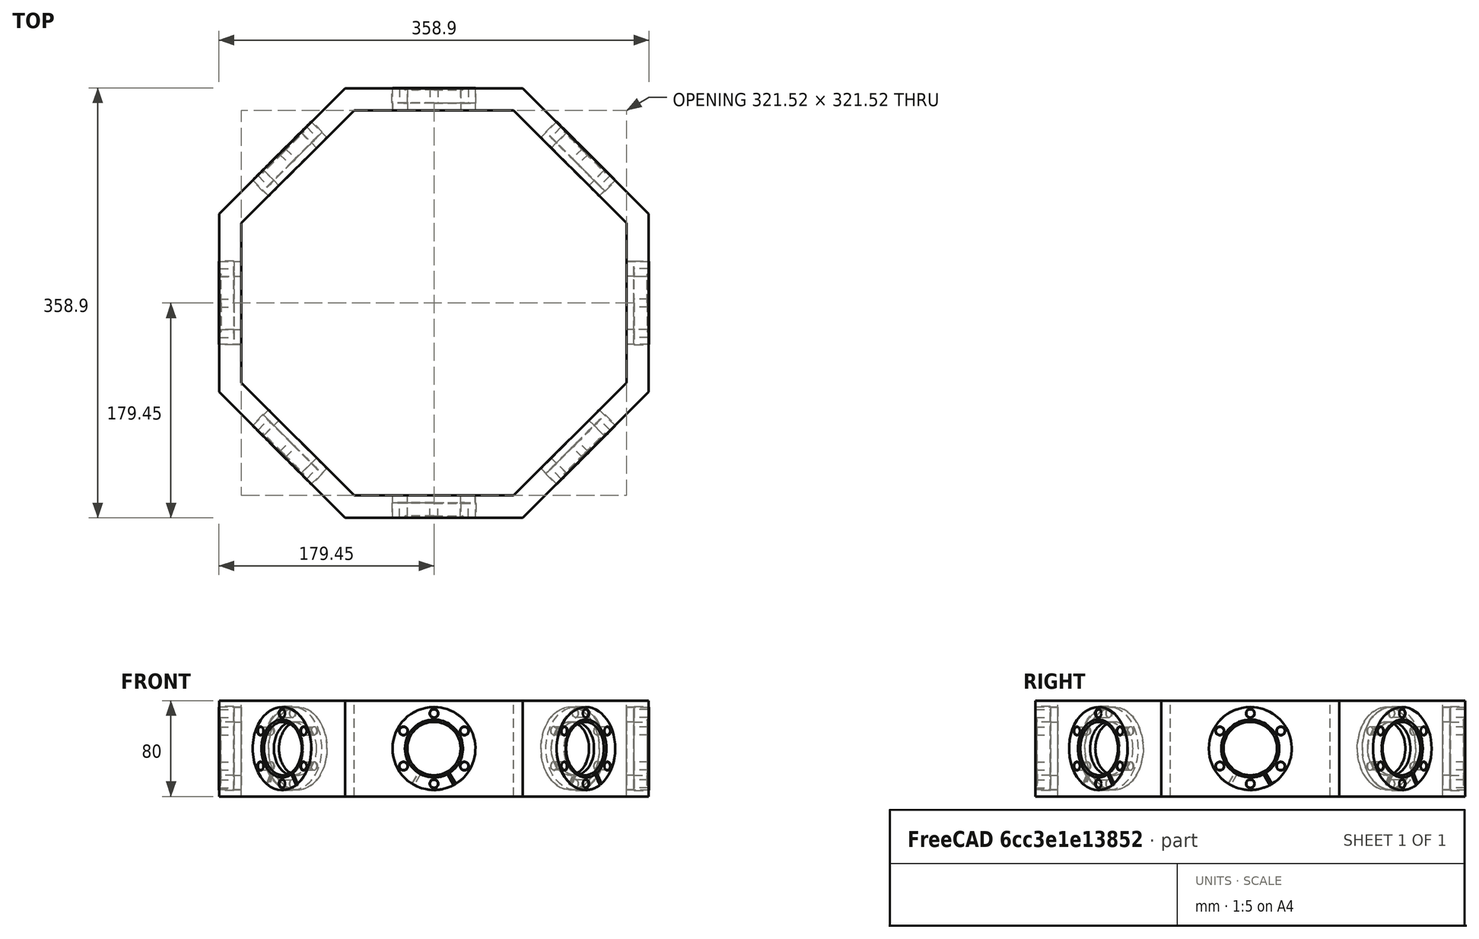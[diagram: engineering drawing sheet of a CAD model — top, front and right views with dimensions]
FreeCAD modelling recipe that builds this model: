
FCSTD DOCUMENT  (FreeCAD 0.20R29603 (Git))
Label: tem_octagon
License: All rights reserved
LicenseURL: http://en.wikipedia.org/wiki/All_rights_reserved
objects: Part::Compound×18, Part::Cylinder×16, Part::Cut×10, Part::Feature×8, Part::FeaturePython×8, Part::Part2DObjectPython×2, Part::Extrusion×2
note: 64 computed .brp shape members not serialized (recipe doc carries the construction recipe); baked Part::Feature solids carry a one-line shape summary decoded from their .brp

FEATURE [Part::Part2DObjectPython] Wire  # Draft 2D object (typed FeaturePython)
  Area = 106458
  ChamferSize = 0
  Closed = true
  End = (74.24,179.24,-40)
  FilletRadius = 0
  Length = 1187.89
  MakeFace = true
  Placement = pos=(0,0,-40) rot=(0,0,1;0rad)
  Points = (9) [(74.24,179.24,-2.13163e-14),(179.24,74.24,0),(179.24,-74.24,0),(74.24,-179.24,0),(-74.24,-179.24,0),(-179.24,-74.24,0),(-179.24,74.24,0),(-74.24,179.24,0),(74.24,179.24,-2.13163e-14)]
  Start = (74.24,179.24,-40)
  Subdivisions = 0
FEATURE [Part::Extrusion] Extrude
  Base = -> Wire
  Dir = (0,0,1)
  DirMode = 2
  FaceMakerClass = Part::FaceMakerBullseye
  LengthFwd = 80
  LengthRev = 0
  Solid = false
  Symmetric = false
FEATURE [Part::Part2DObjectPython] Wire001  # Draft 2D object (typed FeaturePython)
  Area = 85639.1
  ChamferSize = 0
  Closed = true
  End = (66.59,160.76,-40)
  FilletRadius = 0
  Length = 1065.43
  MakeFace = true
  Placement = pos=(0,0,-40) rot=(0,0,1;0rad)
  Points = (9) [(66.59,160.76,0),(160.76,66.59,0),(160.76,-66.59,0),(66.59,-160.76,0),(-66.59,-160.76,0),(-160.76,-66.59,0),(-160.76,66.59,0),(-66.59,160.76,0),(66.59,160.76,0)]
  Start = (66.59,160.76,-40)
  Subdivisions = 0
FEATURE [Part::Extrusion] Extrude001
  Base = -> Wire001
  Dir = (0,0,1)
  DirMode = 2
  FaceMakerClass = Part::FaceMakerBullseye
  LengthFwd = 80
  LengthRev = 0
  Solid = false
  Symmetric = false
FEATURE [Part::Cut] Cut
  Base = -> Extrude
  Tool = -> Extrude001
FEATURE [Part::Feature] Solid  label="Hositrad_CF35-Blank"
  Placement = pos=(0,166.75,0) rot=(0,0,1;0rad)
  shape: bbox 70 x 12.7 x 70 mm, 58 faces (baked)
FEATURE [Part::Cylinder] Cylinder  label="Zylinder"
  Angle = 360
  AttacherType = Attacher::AttachEngine3D
  FirstAngle = 0
  Height = 20
  Placement = pos=(0,179.75,0) rot=(1,0,0;1.5708rad)
  Radius = 34.5
  SecondAngle = 0
FEATURE [Part::Cylinder] Cylinder001  label="Zylinder001"
  Angle = 360
  AttacherType = Attacher::AttachEngine3D
  FirstAngle = 0
  Height = 20
  Placement = pos=(0,179.75,0) rot=(1,0,0;1.5708rad)
  Radius = 22.25
  SecondAngle = 0
FEATURE [Part::Cylinder] Cylinder002  label="Zylinder002"
  Angle = 360
  AttacherType = Attacher::AttachEngine3D
  FirstAngle = 0
  Height = 20
  Placement = pos=(0,179.75,0) rot=(1,0,0;1.5708rad)
  Radius = 34.5
  SecondAngle = 0
FEATURE [Part::Compound] Compound
  Links = -> [Cylinder002]
  Placement = pos=(0,0,0) rot=(0,0,1;0.785398rad)
FEATURE [Part::Cylinder] Cylinder003  label="Zylinder003"
  Angle = 360
  AttacherType = Attacher::AttachEngine3D
  FirstAngle = 0
  Height = 20
  Placement = pos=(0,179.75,0) rot=(1,0,0;1.5708rad)
  Radius = 34.5
  SecondAngle = 0
FEATURE [Part::Compound] Compound001
  Links = -> [Cylinder003]
  Placement = pos=(0,0,0) rot=(0,0,1;1.5708rad)
FEATURE [Part::Cylinder] Cylinder004  label="Zylinder004"
  Angle = 360
  AttacherType = Attacher::AttachEngine3D
  FirstAngle = 0
  Height = 20
  Placement = pos=(0,179.75,0) rot=(1,0,0;1.5708rad)
  Radius = 34.5
  SecondAngle = 0
FEATURE [Part::Compound] Compound002
  Links = -> [Cylinder004]
  Placement = pos=(0,0,0) rot=(0,0,1;2.35619rad)
FEATURE [Part::Cylinder] Cylinder005  label="Zylinder005"
  Angle = 360
  AttacherType = Attacher::AttachEngine3D
  FirstAngle = 0
  Height = 20
  Placement = pos=(0,179.75,0) rot=(1,0,0;1.5708rad)
  Radius = 34.5
  SecondAngle = 0
FEATURE [Part::Compound] Compound003
  Links = -> [Cylinder005]
  Placement = pos=(0,0,0) rot=(0,0,1;3.14159rad)
FEATURE [Part::Cylinder] Cylinder006  label="Zylinder006"
  Angle = 360
  AttacherType = Attacher::AttachEngine3D
  FirstAngle = 0
  Height = 20
  Placement = pos=(0,179.75,0) rot=(1,0,0;1.5708rad)
  Radius = 34.5
  SecondAngle = 0
FEATURE [Part::Compound] Compound004
  Links = -> [Cylinder006]
  Placement = pos=(0,0,0) rot=(0,0,1;3.92699rad)
FEATURE [Part::Cylinder] Cylinder007  label="Zylinder007"
  Angle = 360
  AttacherType = Attacher::AttachEngine3D
  FirstAngle = 0
  Height = 20
  Placement = pos=(0,179.75,0) rot=(1,0,0;1.5708rad)
  Radius = 34.5
  SecondAngle = 0
FEATURE [Part::Compound] Compound005
  Links = -> [Cylinder007]
  Placement = pos=(0,0,0) rot=(0,0,1;4.71239rad)
FEATURE [Part::Cylinder] Cylinder008  label="Zylinder008"
  Angle = 360
  AttacherType = Attacher::AttachEngine3D
  FirstAngle = 0
  Height = 20
  Placement = pos=(0,179.75,0) rot=(1,0,0;1.5708rad)
  Radius = 34.5
  SecondAngle = 0
FEATURE [Part::Compound] Compound006
  Links = -> [Cylinder008]
  Placement = pos=(0,0,0) rot=(0,0,1;5.49779rad)
FEATURE [Part::Compound] Compound007
  Links = -> [Cylinder,Compound,Compound001,Compound002,Compound003,Compound004,Compound005,Compound006]
FEATURE [Part::Cut] Cut001
  Base = -> Cut
  Tool = -> Compound007
FEATURE [Part::Cut] Cut002
  Base = -> Solid
  Tool = -> Cylinder001
FEATURE [Part::FeaturePython] Tube  # WARN: FeaturePython — macro-defined, semantics opaque (R4)
  AttacherType = Attacher::AttachEngine3D
  Height = 6
  InnerRadius = 22.25
  OuterRadius = 34.5
  Placement = pos=(0,166.76,0) rot=(1,0,0;1.5708rad)
FEATURE [Part::Compound] Compound008
  Links = -> [Tube,Cut002]
FEATURE [Part::Cylinder] Cylinder009  label="Zylinder009"
  Angle = 360
  AttacherType = Attacher::AttachEngine3D
  FirstAngle = 0
  Height = 20
  Placement = pos=(0,179.75,0) rot=(1,0,0;1.5708rad)
  Radius = 22.25
  SecondAngle = 0
FEATURE [Part::Feature] Solid001  label="Hositrad_CF35-Blank001"
  Placement = pos=(0,166.75,0) rot=(0,0,1;0rad)
  shape: bbox 70 x 12.7 x 70 mm, 58 faces (baked)
FEATURE [Part::Cut] Cut003
  Base = -> Solid001
  Tool = -> Cylinder009
FEATURE [Part::FeaturePython] Tube001  # WARN: FeaturePython — macro-defined, semantics opaque (R4)
  AttacherType = Attacher::AttachEngine3D
  Height = 6
  InnerRadius = 22.25
  OuterRadius = 34.5
  Placement = pos=(0,166.76,0) rot=(1,0,0;1.5708rad)
FEATURE [Part::Compound] Compound009
  Links = -> [Tube001,Cut003]
  Placement = pos=(0,0,0) rot=(0,0,1;0.785398rad)
FEATURE [Part::Cylinder] Cylinder010  label="Zylinder010"
  Angle = 360
  AttacherType = Attacher::AttachEngine3D
  FirstAngle = 0
  Height = 20
  Placement = pos=(0,179.75,0) rot=(1,0,0;1.5708rad)
  Radius = 22.25
  SecondAngle = 0
FEATURE [Part::Feature] Solid002  label="Hositrad_CF35-Blank002"
  Placement = pos=(0,166.75,0) rot=(0,0,1;0rad)
  shape: bbox 70 x 12.7 x 70 mm, 58 faces (baked)
FEATURE [Part::Cut] Cut004
  Base = -> Solid002
  Tool = -> Cylinder010
FEATURE [Part::FeaturePython] Tube002  # WARN: FeaturePython — macro-defined, semantics opaque (R4)
  AttacherType = Attacher::AttachEngine3D
  Height = 6
  InnerRadius = 22.25
  OuterRadius = 34.5
  Placement = pos=(0,166.76,0) rot=(1,0,0;1.5708rad)
FEATURE [Part::Compound] Compound010
  Links = -> [Tube002,Cut004]
  Placement = pos=(0,0,0) rot=(0,0,1;1.5708rad)
FEATURE [Part::Cylinder] Cylinder011  label="Zylinder011"
  Angle = 360
  AttacherType = Attacher::AttachEngine3D
  FirstAngle = 0
  Height = 20
  Placement = pos=(0,179.75,0) rot=(1,0,0;1.5708rad)
  Radius = 22.25
  SecondAngle = 0
FEATURE [Part::Feature] Solid003  label="Hositrad_CF35-Blank003"
  Placement = pos=(0,166.75,0) rot=(0,0,1;0rad)
  shape: bbox 70 x 12.7 x 70 mm, 58 faces (baked)
FEATURE [Part::Cut] Cut005
  Base = -> Solid003
  Tool = -> Cylinder011
FEATURE [Part::FeaturePython] Tube003  # WARN: FeaturePython — macro-defined, semantics opaque (R4)
  AttacherType = Attacher::AttachEngine3D
  Height = 6
  InnerRadius = 22.25
  OuterRadius = 34.5
  Placement = pos=(0,166.76,0) rot=(1,0,0;1.5708rad)
FEATURE [Part::Compound] Compound011
  Links = -> [Tube003,Cut005]
  Placement = pos=(0,0,0) rot=(0,0,1;2.35619rad)
FEATURE [Part::Cylinder] Cylinder012  label="Zylinder012"
  Angle = 360
  AttacherType = Attacher::AttachEngine3D
  FirstAngle = 0
  Height = 20
  Placement = pos=(0,179.75,0) rot=(1,0,0;1.5708rad)
  Radius = 22.25
  SecondAngle = 0
FEATURE [Part::Feature] Solid004  label="Hositrad_CF35-Blank004"
  Placement = pos=(0,166.75,0) rot=(0,0,1;0rad)
  shape: bbox 70 x 12.7 x 70 mm, 58 faces (baked)
FEATURE [Part::Cut] Cut006
  Base = -> Solid004
  Tool = -> Cylinder012
FEATURE [Part::FeaturePython] Tube004  # WARN: FeaturePython — macro-defined, semantics opaque (R4)
  AttacherType = Attacher::AttachEngine3D
  Height = 6
  InnerRadius = 22.25
  OuterRadius = 34.5
  Placement = pos=(0,166.76,0) rot=(1,0,0;1.5708rad)
FEATURE [Part::Compound] Compound012
  Links = -> [Tube004,Cut006]
  Placement = pos=(0,0,0) rot=(0,0,1;3.14159rad)
FEATURE [Part::Cylinder] Cylinder013  label="Zylinder013"
  Angle = 360
  AttacherType = Attacher::AttachEngine3D
  FirstAngle = 0
  Height = 20
  Placement = pos=(0,179.75,0) rot=(1,0,0;1.5708rad)
  Radius = 22.25
  SecondAngle = 0
FEATURE [Part::Feature] Solid005  label="Hositrad_CF35-Blank005"
  Placement = pos=(0,166.75,0) rot=(0,0,1;0rad)
  shape: bbox 70 x 12.7 x 70 mm, 58 faces (baked)
FEATURE [Part::Cut] Cut007
  Base = -> Solid005
  Tool = -> Cylinder013
FEATURE [Part::FeaturePython] Tube005  # WARN: FeaturePython — macro-defined, semantics opaque (R4)
  AttacherType = Attacher::AttachEngine3D
  Height = 6
  InnerRadius = 22.25
  OuterRadius = 34.5
  Placement = pos=(0,166.76,0) rot=(1,0,0;1.5708rad)
FEATURE [Part::Compound] Compound013
  Links = -> [Tube005,Cut007]
  Placement = pos=(0,0,0) rot=(0,0,1;3.92699rad)
FEATURE [Part::Cylinder] Cylinder014  label="Zylinder014"
  Angle = 360
  AttacherType = Attacher::AttachEngine3D
  FirstAngle = 0
  Height = 20
  Placement = pos=(0,179.75,0) rot=(1,0,0;1.5708rad)
  Radius = 22.25
  SecondAngle = 0
FEATURE [Part::Feature] Solid006  label="Hositrad_CF35-Blank006"
  Placement = pos=(0,166.75,0) rot=(0,0,1;0rad)
  shape: bbox 70 x 12.7 x 70 mm, 58 faces (baked)
FEATURE [Part::Cut] Cut008
  Base = -> Solid006
  Tool = -> Cylinder014
FEATURE [Part::FeaturePython] Tube006  # WARN: FeaturePython — macro-defined, semantics opaque (R4)
  AttacherType = Attacher::AttachEngine3D
  Height = 6
  InnerRadius = 22.25
  OuterRadius = 34.5
  Placement = pos=(0,166.76,0) rot=(1,0,0;1.5708rad)
FEATURE [Part::Compound] Compound014
  Links = -> [Tube006,Cut008]
  Placement = pos=(0,0,0) rot=(0,0,1;4.71239rad)
FEATURE [Part::Cylinder] Cylinder015  label="Zylinder015"
  Angle = 360
  AttacherType = Attacher::AttachEngine3D
  FirstAngle = 0
  Height = 20
  Placement = pos=(0,179.75,0) rot=(1,0,0;1.5708rad)
  Radius = 22.25
  SecondAngle = 0
FEATURE [Part::Feature] Solid007  label="Hositrad_CF35-Blank007"
  Placement = pos=(0,166.75,0) rot=(0,0,1;0rad)
  shape: bbox 70 x 12.7 x 70 mm, 58 faces (baked)
FEATURE [Part::Cut] Cut009
  Base = -> Solid007
  Tool = -> Cylinder015
FEATURE [Part::FeaturePython] Tube007  # WARN: FeaturePython — macro-defined, semantics opaque (R4)
  AttacherType = Attacher::AttachEngine3D
  Height = 6
  InnerRadius = 22.25
  OuterRadius = 34.5
  Placement = pos=(0,166.76,0) rot=(1,0,0;1.5708rad)
FEATURE [Part::Compound] Compound015
  Links = -> [Tube007,Cut009]
  Placement = pos=(0,0,0) rot=(0,0,1;5.49779rad)
FEATURE [Part::Compound] Compound016
  Links = -> [Compound008,Compound009,Compound010,Compound011,Compound012,Compound013,Compound014,Compound015]
FEATURE [Part::Compound] Compound017
  Links = -> [Cut001,Compound016]
